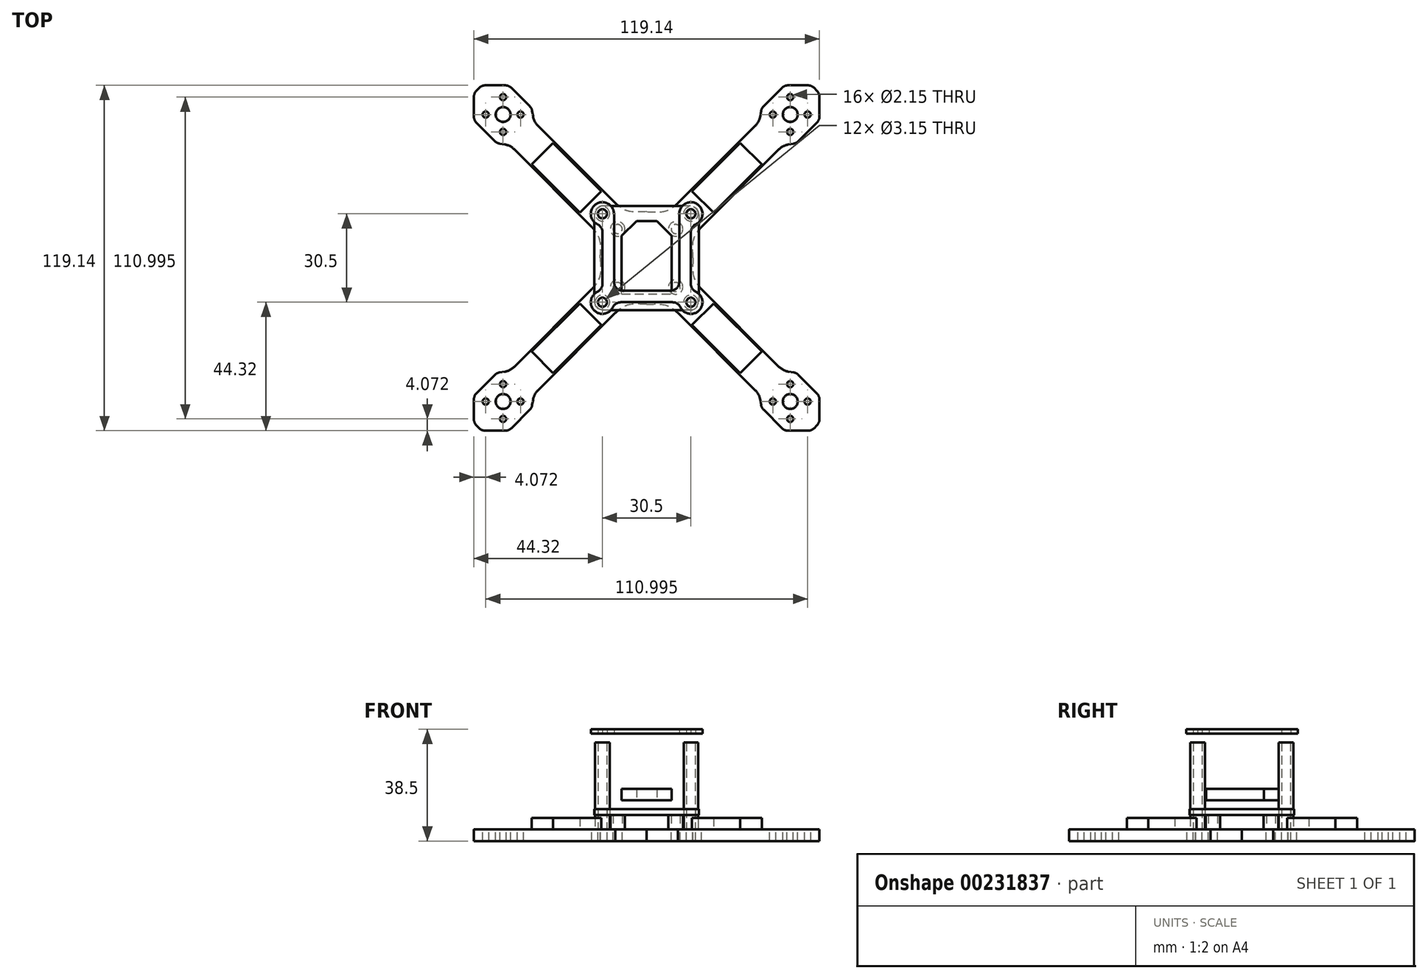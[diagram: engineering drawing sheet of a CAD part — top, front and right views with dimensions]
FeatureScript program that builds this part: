
annotation { "Feature Type Name" : "Feature", "Feature Type Description" : "" }
export const myFeature = defineFeature(function(context is Context, id is Id, definition is map)
    precondition{}
    {
        {
            var Q0;
            Q0=qCreatedBy(makeId("Top.planeOp"),FACE);
            var sketch = newSketch(context, id + "F0", { "sketchPlane" : qUnion([Q0])});
            skCircle(sketch, "E0.1", {"center": v(15.25, 15.25) * mm, "radius": 1.57 * mm});
            skLineSegment(sketch, "E1", {"start": v(49.5, 55.5) * mm, "end": v(49.5, 43.5) * mm, "construction": true});
            skLineSegment(sketch, "E2", {"start": v(45.25, 53.74) * mm, "end": v(53.74, 45.25) * mm, "construction": true});
            skCircle(sketch, "E3.MirrorC", {"center": v(49.5, 49.5) * mm, "radius": 2.58 * mm});
            skLineSegment(sketch, "E4", {"start": v(43.5, 49.5) * mm, "end": v(55.5, 49.5) * mm, "construction": true});
            skCircle(sketch, "E5", {"center": v(49.5, 49.5) * mm, "radius": 6 * mm, "construction": true});
            skCircle(sketch, "E6", {"center": v(43.5, 49.5) * mm, "radius": 1.07 * mm});
            skCircle(sketch, "E7.MirrorC", {"center": v(55.5, 49.5) * mm, "radius": 1.07 * mm});
            skCircle(sketch, "E8.MirrorC", {"center": v(49.5, 55.5) * mm, "radius": 1.07 * mm});
            skCircle(sketch, "E9.MirrorC", {"center": v(49.5, 43.5) * mm, "radius": 1.07 * mm});
            skLineSegment(sketch, "E10", {"start": v(0, 78.07) * mm, "end": v(0, -78.07) * mm, "construction": true});
            skLineSegment(sketch, "E11", {"start": v(-70, 0) * mm, "end": v(70, 0) * mm, "construction": true});
            skCircle(sketch, "E12.MirrorC", {"center": v(-15.25, 15.25) * mm, "radius": 1.57 * mm});
            skCircle(sketch, "E13.MirrorC", {"center": v(-15.25, -15.25) * mm, "radius": 1.57 * mm});
            skCircle(sketch, "E14.MirrorC", {"center": v(15.25, -15.25) * mm, "radius": 1.57 * mm});
            skLineSegment(sketch, "E15", {"start": v(49.5, 49.5) * mm, "end": v(-49.5, -49.5) * mm, "construction": true});
            skLineSegment(sketch, "E16", {"start": v(-49.5, 49.5) * mm, "end": v(49.5, -49.5) * mm, "construction": true});
            skLineSegment(sketch, "E17", {"start": v(10.78, 18.91) * mm, "end": v(18.91, 10.78) * mm, "construction": true});
            skPoint(sketch, "E18", {"position": v(14.85, 14.85) * mm});
            skPoint(sketch, "E19", {"position": v(0, 16) * mm});
            skLineSegment(sketch, "E20", {"start": v(49.5, 49.5) * mm, "end": v(67.48, 67.48) * mm, "construction": true});
            skCircle(sketch, "E21.MirrorC", {"center": v(55.5, -49.5) * mm, "radius": 1.07 * mm});
            skCircle(sketch, "E22.MirrorC", {"center": v(49.5, -43.5) * mm, "radius": 1.07 * mm});
            skLineSegment(sketch, "E23.MirrorCS", {"start": v(45.25, -53.74) * mm, "end": v(53.74, -45.25) * mm, "construction": true});
            skCircle(sketch, "E24.MirrorC", {"center": v(49.5, -55.5) * mm, "radius": 1.07 * mm});
            skLineSegment(sketch, "E25.MirrorCS", {"start": v(49.5, -55.5) * mm, "end": v(49.5, -43.5) * mm, "construction": true});
            skLineSegment(sketch, "E26.MirrorCS", {"start": v(43.5, -49.5) * mm, "end": v(55.5, -49.5) * mm, "construction": true});
            skCircle(sketch, "E27.MirrorC", {"center": v(43.5, -49.5) * mm, "radius": 1.07 * mm});
            skPoint(sketch, "E28.MirrorP", {"position": v(49.5, -49.5) * mm});
            skCircle(sketch, "E29.MirrorC", {"center": v(49.5, -49.5) * mm, "radius": 6 * mm, "construction": true});
            skCircle(sketch, "E30.MirrorC", {"center": v(49.5, -49.5) * mm, "radius": 2.58 * mm});
            skCircle(sketch, "E31.MirrorC", {"center": v(-49.5, -55.5) * mm, "radius": 1.07 * mm});
            skCircle(sketch, "E32.MirrorC", {"center": v(-43.5, -49.5) * mm, "radius": 1.07 * mm});
            skCircle(sketch, "E33.MirrorC", {"center": v(-55.5, -49.5) * mm, "radius": 1.07 * mm});
            skCircle(sketch, "E34.MirrorC", {"center": v(-49.5, -43.5) * mm, "radius": 1.07 * mm});
            skLineSegment(sketch, "E35.MirrorCS", {"start": v(-45.25, -53.74) * mm, "end": v(-53.74, -45.25) * mm, "construction": true});
            skLineSegment(sketch, "E36.MirrorCS", {"start": v(-43.5, -49.5) * mm, "end": v(-55.5, -49.5) * mm, "construction": true});
            skLineSegment(sketch, "E37.MirrorCS", {"start": v(-49.5, -55.5) * mm, "end": v(-49.5, -43.5) * mm, "construction": true});
            skPoint(sketch, "E38.MirrorP", {"position": v(-49.5, -49.5) * mm});
            skCircle(sketch, "E39.MirrorC", {"center": v(-49.5, -49.5) * mm, "radius": 6 * mm, "construction": true});
            skCircle(sketch, "E40.MirrorC", {"center": v(-49.5, -49.5) * mm, "radius": 2.58 * mm});
            skCircle(sketch, "E41.MirrorC", {"center": v(-49.5, 55.5) * mm, "radius": 1.07 * mm});
            skCircle(sketch, "E42.MirrorC", {"center": v(-43.5, 49.5) * mm, "radius": 1.07 * mm});
            skCircle(sketch, "E43.MirrorC", {"center": v(-49.5, 43.5) * mm, "radius": 1.07 * mm});
            skCircle(sketch, "E44.MirrorC", {"center": v(-55.5, 49.5) * mm, "radius": 1.07 * mm});
            skLineSegment(sketch, "E45.MirrorCS", {"start": v(-45.25, 53.74) * mm, "end": v(-53.74, 45.25) * mm, "construction": true});
            skLineSegment(sketch, "E46.MirrorCS", {"start": v(-43.5, 49.5) * mm, "end": v(-55.5, 49.5) * mm, "construction": true});
            skLineSegment(sketch, "E47.MirrorCS", {"start": v(-49.5, 55.5) * mm, "end": v(-49.5, 43.5) * mm, "construction": true});
            skPoint(sketch, "E48.MirrorP", {"position": v(-49.5, 49.5) * mm});
            skCircle(sketch, "E49.MirrorC", {"center": v(-49.5, 49.5) * mm, "radius": 6 * mm, "construction": true});
            skCircle(sketch, "E50.MirrorC", {"center": v(-49.5, 49.5) * mm, "radius": 2.58 * mm});
            skCircle(sketch, "E51.MirrorC", {"center": v(10, 10) * mm, "radius": 1.57 * mm});
            skCircle(sketch, "E52.MirrorC", {"center": v(10, -10) * mm, "radius": 1.57 * mm});
            skCircle(sketch, "E53.MirrorC", {"center": v(-10, -10) * mm, "radius": 1.57 * mm});
            skCircle(sketch, "E54.MirrorC", {"center": v(-10, 10) * mm, "radius": 1.57 * mm});
            skLineSegment(sketch, "E55", {"start": v(16, 8) * mm, "end": v(16, -8) * mm, "construction": true});
            skPoint(sketch, "E56", {"position": v(16, 0) * mm});
            skPoint(sketch, "E57", {"position": v(0, 0) * mm});
            skPoint(sketch, "E58", {"position": v(-27.66, 27.66) * mm});
            skPoint(sketch, "E59", {"position": v(6.88, 16.35) * mm});
            skFitSpline(sketch, "E60", {"points": [v(0, 16) * mm, v(6.88, 16.35) * mm, v(10.78, 18.91) * mm], "startDerivative": vector(12.86, -0.37) * mm, "endDerivative": vector(5.42, 4.33) * mm});
            skLineSegment(sketch, "E61", {"start": v(10.78, 18.91) * mm, "end": v(37.5, 45.63) * mm});
            skLineSegment(sketch, "E62", {"start": v(39.18, 48.92) * mm, "end": v(39.46, 50.68) * mm});
            skLineSegment(sketch, "E63", {"start": v(40.3, 52.33) * mm, "end": v(46.67, 58.69) * mm});
            skLineSegment(sketch, "E64", {"start": v(48.8, 59.57) * mm, "end": v(55.6, 59.57) * mm});
            skLineSegment(sketch, "E65", {"start": v(57.71, 58.69) * mm, "end": v(58.2, 58.2) * mm});
            skPoint(sketch, "E66.visualSharp", {"position": v(38.87, 47) * mm});
            skArc(sketch, "E66.filletArc", {"start": v(37.5, 45.63) * mm, "mid": v(38.6, 47.14) * mm, "end": v(39.18, 48.92) * mm});
            skPoint(sketch, "E67.visualSharp", {"position": v(39.62, 51.64) * mm});
            skArc(sketch, "E67.filletArc", {"start": v(40.3, 52.33) * mm, "mid": v(39.76, 51.57) * mm, "end": v(39.46, 50.68) * mm});
            skPoint(sketch, "E68.visualSharp", {"position": v(47.55, 59.57) * mm});
            skArc(sketch, "E68.filletArc", {"start": v(48.8, 59.57) * mm, "mid": v(47.64, 59.34) * mm, "end": v(46.67, 58.69) * mm});
            skPoint(sketch, "E69.visualSharp", {"position": v(56.84, 59.57) * mm});
            skArc(sketch, "E69.filletArc", {"start": v(57.71, 58.69) * mm, "mid": v(56.74, 59.34) * mm, "end": v(55.6, 59.57) * mm});
            skLineSegment(sketch, "E70.MirrorCS", {"start": v(52.33, 40.3) * mm, "end": v(58.69, 46.67) * mm});
            skPoint(sketch, "E71.MirrorP", {"position": v(47, 38.87) * mm});
            skArc(sketch, "E72.MirrorCS", {"start": v(52.33, 40.3) * mm, "mid": v(51.57, 39.76) * mm, "end": v(50.68, 39.46) * mm});
            skArc(sketch, "E73.MirrorCS", {"start": v(45.63, 37.5) * mm, "mid": v(47.14, 38.6) * mm, "end": v(48.92, 39.18) * mm});
            skPoint(sketch, "E74.MirrorP", {"position": v(51.64, 39.62) * mm});
            skArc(sketch, "E75.MirrorCS", {"start": v(59.57, 48.8) * mm, "mid": v(59.34, 47.64) * mm, "end": v(58.69, 46.67) * mm});
            skArc(sketch, "E76.MirrorCS", {"start": v(58.69, 57.71) * mm, "mid": v(59.34, 56.74) * mm, "end": v(59.57, 55.6) * mm});
            skPoint(sketch, "E77.MirrorP", {"position": v(59.57, 56.84) * mm});
            skLineSegment(sketch, "E78.MirrorCS", {"start": v(58.69, 57.71) * mm, "end": v(58.2, 58.2) * mm});
            skLineSegment(sketch, "E79.MirrorCS", {"start": v(59.57, 48.8) * mm, "end": v(59.57, 55.6) * mm});
            skPoint(sketch, "E80.MirrorP", {"position": v(59.57, 47.55) * mm});
            skLineSegment(sketch, "E81.MirrorCS", {"start": v(18.91, 10.78) * mm, "end": v(45.63, 37.5) * mm});
            skLineSegment(sketch, "E82.MirrorCS", {"start": v(48.92, 39.18) * mm, "end": v(50.68, 39.46) * mm});
            skFitSpline(sketch, "E83.MirrorCS", {"points": [v(16, 0) * mm, v(16.35, 6.88) * mm, v(18.91, 10.78) * mm], "startDerivative": vector(-0.37, 12.86) * mm, "endDerivative": vector(4.33, 5.42) * mm});
            skLineSegment(sketch, "E84", {"start": v(48.8, 56.57) * mm, "end": v(42.43, 50.2) * mm, "construction": true});
            skPoint(sketch, "E85", {"position": v(45.6, 53.39) * mm});
            skLineSegment(sketch, "E86.MirrorCS", {"start": v(57.71, -58.69) * mm, "end": v(58.2, -58.2) * mm});
            skLineSegment(sketch, "E87.MirrorCS", {"start": v(48.92, -39.18) * mm, "end": v(50.68, -39.46) * mm});
            skLineSegment(sketch, "E88.MirrorCS", {"start": v(39.18, -48.92) * mm, "end": v(39.46, -50.68) * mm});
            skLineSegment(sketch, "E89.MirrorCS", {"start": v(58.69, -57.71) * mm, "end": v(58.2, -58.2) * mm});
            skArc(sketch, "E90.MirrorCS", {"start": v(48.8, -59.57) * mm, "mid": v(47.64, -59.34) * mm, "end": v(46.67, -58.69) * mm});
            skArc(sketch, "E91.MirrorCS", {"start": v(37.5, -45.63) * mm, "mid": v(38.6, -47.14) * mm, "end": v(39.18, -48.92) * mm});
            skArc(sketch, "E92.MirrorCS", {"start": v(57.71, -58.69) * mm, "mid": v(56.74, -59.34) * mm, "end": v(55.6, -59.57) * mm});
            skArc(sketch, "E93.MirrorCS", {"start": v(45.63, -37.5) * mm, "mid": v(47.14, -38.6) * mm, "end": v(48.92, -39.18) * mm});
            skArc(sketch, "E94.MirrorCS", {"start": v(59.57, -48.8) * mm, "mid": v(59.34, -47.64) * mm, "end": v(58.69, -46.67) * mm});
            skArc(sketch, "E95.MirrorCS", {"start": v(52.33, -40.3) * mm, "mid": v(51.57, -39.76) * mm, "end": v(50.68, -39.46) * mm});
            skArc(sketch, "E96.MirrorCS", {"start": v(58.69, -57.71) * mm, "mid": v(59.34, -56.74) * mm, "end": v(59.57, -55.6) * mm});
            skArc(sketch, "E97.MirrorCS", {"start": v(40.3, -52.33) * mm, "mid": v(39.76, -51.57) * mm, "end": v(39.46, -50.68) * mm});
            skLineSegment(sketch, "E98.MirrorCS", {"start": v(48.8, -56.57) * mm, "end": v(42.43, -50.2) * mm, "construction": true});
            skFitSpline(sketch, "E99.MirrorCS", {"points": [v(16, 0) * mm, v(16.35, -6.88) * mm, v(18.91, -10.78) * mm], "startDerivative": vector(-0.37, -12.86) * mm, "endDerivative": vector(4.33, -5.42) * mm});
            skFitSpline(sketch, "E100.MirrorCS", {"points": [v(0, -16) * mm, v(6.88, -16.35) * mm, v(10.78, -18.91) * mm], "startDerivative": vector(12.86, 0.37) * mm, "endDerivative": vector(5.42, -4.33) * mm});
            skPoint(sketch, "E101.MirrorP", {"position": v(59.57, -47.55) * mm});
            skLineSegment(sketch, "E102.MirrorCS", {"start": v(52.33, -40.3) * mm, "end": v(58.69, -46.67) * mm});
            skLineSegment(sketch, "E103.MirrorCS", {"start": v(40.3, -52.33) * mm, "end": v(46.67, -58.69) * mm});
            skPoint(sketch, "E104.MirrorP", {"position": v(47.55, -59.57) * mm});
            skPoint(sketch, "E105.MirrorP", {"position": v(38.87, -47) * mm});
            skPoint(sketch, "E106.MirrorP", {"position": v(47, -38.87) * mm});
            skLineSegment(sketch, "E107.MirrorCS", {"start": v(10.78, -18.91) * mm, "end": v(37.5, -45.63) * mm});
            skPoint(sketch, "E108.MirrorP", {"position": v(39.62, -51.64) * mm});
            skLineSegment(sketch, "E109.MirrorCS", {"start": v(59.57, -48.8) * mm, "end": v(59.57, -55.6) * mm});
            skPoint(sketch, "E110.MirrorP", {"position": v(51.64, -39.62) * mm});
            skPoint(sketch, "E111.MirrorP", {"position": v(59.57, -56.84) * mm});
            skPoint(sketch, "E112.MirrorP", {"position": v(45.6, -53.39) * mm});
            skLineSegment(sketch, "E113.MirrorCS", {"start": v(48.8, -59.57) * mm, "end": v(55.6, -59.57) * mm});
            skPoint(sketch, "E114.MirrorP", {"position": v(56.84, -59.57) * mm});
            skLineSegment(sketch, "E115.MirrorCS", {"start": v(18.91, -10.78) * mm, "end": v(45.63, -37.5) * mm});
            skLineSegment(sketch, "E116.MirrorCS", {"start": v(-57.71, 58.69) * mm, "end": v(-58.2, 58.2) * mm});
            skLineSegment(sketch, "E117.MirrorCS", {"start": v(-58.69, -57.71) * mm, "end": v(-58.2, -58.2) * mm});
            skLineSegment(sketch, "E118.MirrorCS", {"start": v(-39.18, -48.92) * mm, "end": v(-39.46, -50.68) * mm});
            skArc(sketch, "E119.MirrorCS", {"start": v(-40.3, -52.33) * mm, "mid": v(-39.76, -51.57) * mm, "end": v(-39.46, -50.68) * mm});
            skArc(sketch, "E120.MirrorCS", {"start": v(-37.5, -45.63) * mm, "mid": v(-38.6, -47.14) * mm, "end": v(-39.18, -48.92) * mm});
            skArc(sketch, "E121.MirrorCS", {"start": v(-45.63, -37.5) * mm, "mid": v(-47.14, -38.6) * mm, "end": v(-48.92, -39.18) * mm});
            skLineSegment(sketch, "E122.MirrorCS", {"start": v(-39.18, 48.92) * mm, "end": v(-39.46, 50.68) * mm});
            skArc(sketch, "E123.MirrorCS", {"start": v(-59.57, -48.8) * mm, "mid": v(-59.34, -47.64) * mm, "end": v(-58.69, -46.67) * mm});
            skArc(sketch, "E124.MirrorCS", {"start": v(-58.69, 57.71) * mm, "mid": v(-59.34, 56.74) * mm, "end": v(-59.57, 55.6) * mm});
            skArc(sketch, "E125.MirrorCS", {"start": v(-57.71, -58.69) * mm, "mid": v(-56.74, -59.34) * mm, "end": v(-55.6, -59.57) * mm});
            skArc(sketch, "E126.MirrorCS", {"start": v(-57.71, 58.69) * mm, "mid": v(-56.74, 59.34) * mm, "end": v(-55.6, 59.57) * mm});
            skLineSegment(sketch, "E127.MirrorCS", {"start": v(-57.71, -58.69) * mm, "end": v(-58.2, -58.2) * mm});
            skLineSegment(sketch, "E128.MirrorCS", {"start": v(-48.92, 39.18) * mm, "end": v(-50.68, 39.46) * mm});
            skLineSegment(sketch, "E129.MirrorCS", {"start": v(-48.92, -39.18) * mm, "end": v(-50.68, -39.46) * mm});
            skLineSegment(sketch, "E130.MirrorCS", {"start": v(-58.69, 57.71) * mm, "end": v(-58.2, 58.2) * mm});
            skArc(sketch, "E131.MirrorCS", {"start": v(-59.57, 48.8) * mm, "mid": v(-59.34, 47.64) * mm, "end": v(-58.69, 46.67) * mm});
            skArc(sketch, "E132.MirrorCS", {"start": v(-40.3, 52.33) * mm, "mid": v(-39.76, 51.57) * mm, "end": v(-39.46, 50.68) * mm});
            skArc(sketch, "E133.MirrorCS", {"start": v(-45.63, 37.5) * mm, "mid": v(-47.14, 38.6) * mm, "end": v(-48.92, 39.18) * mm});
            skArc(sketch, "E134.MirrorCS", {"start": v(-58.69, -57.71) * mm, "mid": v(-59.34, -56.74) * mm, "end": v(-59.57, -55.6) * mm});
            skArc(sketch, "E135.MirrorCS", {"start": v(-52.33, -40.3) * mm, "mid": v(-51.57, -39.76) * mm, "end": v(-50.68, -39.46) * mm});
            skArc(sketch, "E136.MirrorCS", {"start": v(-48.8, 59.57) * mm, "mid": v(-47.64, 59.34) * mm, "end": v(-46.67, 58.69) * mm});
            skArc(sketch, "E137.MirrorCS", {"start": v(-48.8, -59.57) * mm, "mid": v(-47.64, -59.34) * mm, "end": v(-46.67, -58.69) * mm});
            skArc(sketch, "E138.MirrorCS", {"start": v(-37.5, 45.63) * mm, "mid": v(-38.6, 47.14) * mm, "end": v(-39.18, 48.92) * mm});
            skArc(sketch, "E139.MirrorCS", {"start": v(-52.33, 40.3) * mm, "mid": v(-51.57, 39.76) * mm, "end": v(-50.68, 39.46) * mm});
            skFitSpline(sketch, "E140.MirrorCS", {"points": [v(-16, 0) * mm, v(-16.35, 6.88) * mm, v(-18.91, 10.78) * mm], "startDerivative": vector(0.37, 12.86) * mm, "endDerivative": vector(-4.33, 5.42) * mm});
            skFitSpline(sketch, "E141.MirrorCS", {"points": [v(0, -16) * mm, v(-6.88, -16.35) * mm, v(-10.78, -18.91) * mm], "startDerivative": vector(-12.86, 0.37) * mm, "endDerivative": vector(-5.42, -4.33) * mm});
            skLineSegment(sketch, "E142.MirrorCS", {"start": v(-48.8, -56.57) * mm, "end": v(-42.43, -50.2) * mm, "construction": true});
            skFitSpline(sketch, "E143.MirrorCS", {"points": [v(0, 16) * mm, v(-6.88, 16.35) * mm, v(-10.78, 18.91) * mm], "startDerivative": vector(-12.86, -0.37) * mm, "endDerivative": vector(-5.42, 4.33) * mm});
            skFitSpline(sketch, "E144.MirrorCS", {"points": [v(-16, 0) * mm, v(-16.35, -6.88) * mm, v(-18.91, -10.78) * mm], "startDerivative": vector(0.37, -12.86) * mm, "endDerivative": vector(-4.33, -5.42) * mm});
            skLineSegment(sketch, "E145.MirrorCS", {"start": v(-48.8, 56.57) * mm, "end": v(-42.43, 50.2) * mm, "construction": true});
            skLineSegment(sketch, "E146.MirrorCS", {"start": v(-40.3, -52.33) * mm, "end": v(-46.67, -58.69) * mm});
            skLineSegment(sketch, "E147.MirrorCS", {"start": v(-48.8, -59.57) * mm, "end": v(-55.6, -59.57) * mm});
            skPoint(sketch, "E148.MirrorP", {"position": v(-39.62, 51.64) * mm});
            skPoint(sketch, "E149.MirrorP", {"position": v(-47.55, -59.57) * mm});
            skPoint(sketch, "E150.MirrorP", {"position": v(-45.6, -53.39) * mm});
            skLineSegment(sketch, "E151.MirrorCS", {"start": v(-49.5, 49.5) * mm, "end": v(-67.48, 67.48) * mm, "construction": true});
            skPoint(sketch, "E152.MirrorP", {"position": v(-38.87, 47) * mm});
            skLineSegment(sketch, "E153.MirrorCS", {"start": v(-10.78, 18.91) * mm, "end": v(-37.5, 45.63) * mm});
            skLineSegment(sketch, "E154.MirrorCS", {"start": v(-40.3, 52.33) * mm, "end": v(-46.67, 58.69) * mm});
            skPoint(sketch, "E155.MirrorP", {"position": v(-51.64, -39.62) * mm});
            skPoint(sketch, "E156.MirrorP", {"position": v(-59.57, 47.55) * mm});
            skLineSegment(sketch, "E157.MirrorCS", {"start": v(-52.33, -40.3) * mm, "end": v(-58.69, -46.67) * mm});
            skPoint(sketch, "E158.MirrorP", {"position": v(-56.84, 59.57) * mm});
            skPoint(sketch, "E159.MirrorP", {"position": v(-59.57, -47.55) * mm});
            skPoint(sketch, "E160.MirrorP", {"position": v(-59.57, 56.84) * mm});
            skLineSegment(sketch, "E161.MirrorCS", {"start": v(-18.91, 10.78) * mm, "end": v(-45.63, 37.5) * mm});
            skPoint(sketch, "E162.MirrorP", {"position": v(-38.87, -47) * mm});
            skLineSegment(sketch, "E163.MirrorCS", {"start": v(-59.57, 48.8) * mm, "end": v(-59.57, 55.6) * mm});
            skPoint(sketch, "E164.MirrorP", {"position": v(-47, -38.87) * mm});
            skPoint(sketch, "E165.MirrorP", {"position": v(-59.57, -56.84) * mm});
            skLineSegment(sketch, "E166.MirrorCS", {"start": v(-18.91, -10.78) * mm, "end": v(-45.63, -37.5) * mm});
            skPoint(sketch, "E167.MirrorP", {"position": v(-47, 38.87) * mm});
            skPoint(sketch, "E168.MirrorP", {"position": v(-47.55, 59.57) * mm});
            skLineSegment(sketch, "E169.MirrorCS", {"start": v(-52.33, 40.3) * mm, "end": v(-58.69, 46.67) * mm});
            skPoint(sketch, "E170.MirrorP", {"position": v(-56.84, -59.57) * mm});
            skLineSegment(sketch, "E171.MirrorCS", {"start": v(-10.78, -18.91) * mm, "end": v(-37.5, -45.63) * mm});
            skPoint(sketch, "E172.MirrorP", {"position": v(-51.64, 39.62) * mm});
            skLineSegment(sketch, "E173.MirrorCS", {"start": v(-59.57, -48.8) * mm, "end": v(-59.57, -55.6) * mm});
            skLineSegment(sketch, "E174.MirrorCS", {"start": v(-48.8, 59.57) * mm, "end": v(-55.6, 59.57) * mm});
            skPoint(sketch, "E175.MirrorP", {"position": v(-39.62, -51.64) * mm});
            skPoint(sketch, "E176.MirrorP", {"position": v(-45.6, 53.39) * mm});
            skLineSegment(sketch, "E177", {"start": v(45.25, 53.74) * mm, "end": v(40.94, 58.06) * mm, "construction": true});
            skPoint(sketch, "E178", {"position": v(43.49, 55.5) * mm});
            skSolve(sketch);
        }
        {
            var Q0;
            Q0=qCreatedBy(makeId("Top.planeOp"),FACE);
            cPlane(context, id + "F1", {"entities" : qUnion([Q0]), "cplaneType" : CPlaneType.OFFSET, "offset" : 20 * mm, "width" : 150 * mm, "height" : 150 * mm});
        }
        {
            var Q0;
            Q0 = qSketchRegion(id + "F0", true);
            extrude(context, id + "F2", {"entities" : qUnion([Q0]), "oppositeDirection" : true, "depth" : 4 * mm, "offsetDistance" : 25 * mm});
        }
        {
            var Q0;
            Q0=qCreatedBy(makeId("Top.planeOp"),FACE);
            cPlane(context, id + "F3", {"entities" : qUnion([Q0]), "cplaneType" : CPlaneType.OFFSET, "offset" : 10 * mm, "width" : 150 * mm, "height" : 150 * mm});
        }
        {
            var Q0;
            Q0=qCreatedBy(id+"F3.planeOp",FACE);
            var sketch = newSketch(context, id + "F4", { "sketchPlane" : qUnion([Q0])});
            skLineSegment(sketch, "E179", {"start": v(-8.62, -12.37) * mm, "end": v(8.63, -12.37) * mm});
            skLineSegment(sketch, "E180", {"start": v(-8.62, -12.37) * mm, "end": v(-8.62, 7.63) * mm});
            skLineSegment(sketch, "E181", {"start": v(0, -12.37) * mm, "end": v(0, 12.78) * mm, "construction": true});
            skPoint(sketch, "E181.startSnap0", {"position": v(0, -12.37) * mm});
            skLineSegment(sketch, "E182", {"start": v(-3.5, 12.78) * mm, "end": v(3.5, 12.78) * mm});
            skPoint(sketch, "E183", {"position": v(0, 12.78) * mm});
            skLineSegment(sketch, "E184", {"start": v(-8.62, 7.63) * mm, "end": v(-3.5, 12.78) * mm});
            skLineSegment(sketch, "E185.MirrorCS", {"start": v(8.63, 7.63) * mm, "end": v(3.5, 12.78) * mm});
            skLineSegment(sketch, "E186.MirrorCS", {"start": v(8.63, -12.37) * mm, "end": v(8.63, 7.63) * mm});
            skSolve(sketch);
        }
        {
            var Q0;
            Q0 = qSketchRegion(id + "F4", true);
            extrude(context, id + "F5", {"entities" : qUnion([Q0]), "depth" : 4 * mm});
        }
        {
            var Q0;
            Q0=qCreatedBy(makeId("Top.planeOp"),FACE);
            cPlane(context, id + "F6", {"entities" : qUnion([Q0]), "cplaneType" : CPlaneType.OFFSET, "offset" : 5 * mm, "width" : 150 * mm, "height" : 150 * mm});
        }
        {
            var Q0;
            Q0=qCreatedBy(id+"F6.planeOp",FACE);
            var sketch = newSketch(context, id + "F7", { "sketchPlane" : qUnion([Q0])});
            skLineSegment(sketch, "E187", {"start": v(0, 13.5) * mm, "end": v(0, -13.5) * mm, "construction": true});
            skLineSegment(sketch, "E188", {"start": v(-13.5, 0) * mm, "end": v(13.5, 0) * mm, "construction": true});
            skLineSegment(sketch, "E189", {"start": v(-13.5, 10.5) * mm, "end": v(-13.5, -10.5) * mm});
            skLineSegment(sketch, "E190", {"start": v(10.5, 13.5) * mm, "end": v(-10.5, 13.5) * mm});
            skLineSegment(sketch, "E191.MirrorCS", {"start": v(10.5, -13.5) * mm, "end": v(-10.5, -13.5) * mm});
            skLineSegment(sketch, "E192.MirrorCS", {"start": v(13.5, 10.5) * mm, "end": v(13.5, -10.5) * mm});
            skLineSegment(sketch, "E193", {"start": v(-10.5, 13.5) * mm, "end": v(-13.5, 10.5) * mm});
            skLineSegment(sketch, "E194.MirrorCS", {"start": v(-10.5, -13.5) * mm, "end": v(-13.5, -10.5) * mm});
            skLineSegment(sketch, "E195.MirrorCS", {"start": v(10.5, 13.5) * mm, "end": v(13.5, 10.5) * mm});
            skLineSegment(sketch, "E196.MirrorCS", {"start": v(10.5, -13.5) * mm, "end": v(13.5, -10.5) * mm});
            skCircle(sketch, "E197", {"center": v(-10, 10) * mm, "radius": 1.57 * mm});
            skLineSegment(sketch, "E198", {"start": v(-10, 10) * mm, "end": v(10, 10) * mm, "construction": true});
            skLineSegment(sketch, "E199", {"start": v(10, 10) * mm, "end": v(10, -10) * mm, "construction": true});
            skLineSegment(sketch, "E200", {"start": v(10, -10) * mm, "end": v(-10, -10) * mm, "construction": true});
            skLineSegment(sketch, "E201", {"start": v(-10, -10) * mm, "end": v(-10, 10) * mm, "construction": true});
            skPoint(sketch, "E202", {"position": v(0, 10) * mm});
            skPoint(sketch, "E203", {"position": v(-10, 0) * mm});
            skCircle(sketch, "E204.MirrorC", {"center": v(10, 10) * mm, "radius": 1.57 * mm});
            skCircle(sketch, "E205.MirrorC", {"center": v(-10, -10) * mm, "radius": 1.57 * mm});
            skCircle(sketch, "E206.MirrorC", {"center": v(10, -10) * mm, "radius": 1.57 * mm});
            skSolve(sketch);
        }
        {
            var Q0;
            Q0 = qSketchRegion(id + "F7", true);
            extrude(context, id + "F8", {"entities" : qUnion([Q0]), "depth" : 2 * mm});
        }
        {
            var Q0;
            Q0=qCreatedBy(id+"F6.planeOp",FACE);
            var sketch = newSketch(context, id + "F9", { "sketchPlane" : qUnion([Q0])});
            skLineSegment(sketch, "E207", {"start": v(0, 18) * mm, "end": v(0, -18) * mm, "construction": true});
            skLineSegment(sketch, "E208", {"start": v(-18, 0) * mm, "end": v(18, 0) * mm, "construction": true});
            skCircle(sketch, "E209", {"center": v(-15.25, 15.25) * mm, "radius": 1.57 * mm});
            skLineSegment(sketch, "E210", {"start": v(-15.25, 15.25) * mm, "end": v(15.25, 15.25) * mm, "construction": true});
            skLineSegment(sketch, "E211", {"start": v(15.25, 15.25) * mm, "end": v(15.25, -15.25) * mm, "construction": true});
            skLineSegment(sketch, "E212", {"start": v(15.25, -15.25) * mm, "end": v(-15.25, -15.25) * mm, "construction": true});
            skLineSegment(sketch, "E213", {"start": v(-15.25, -15.25) * mm, "end": v(-15.25, 15.25) * mm, "construction": true});
            skPoint(sketch, "E214", {"position": v(0, 15.25) * mm});
            skPoint(sketch, "E215", {"position": v(-15.25, 0) * mm});
            skCircle(sketch, "E216.MirrorC", {"center": v(15.25, 15.25) * mm, "radius": 1.57 * mm});
            skCircle(sketch, "E217.MirrorC", {"center": v(-15.25, -15.25) * mm, "radius": 1.57 * mm});
            skCircle(sketch, "E218.MirrorC", {"center": v(15.25, -15.25) * mm, "radius": 1.57 * mm});
            skPoint(sketch, "E219", {"position": v(0, 0) * mm});
            skLineSegment(sketch, "E220.bottom", {"start": v(15, 18) * mm, "end": v(-15, 18) * mm});
            skLineSegment(sketch, "E220.top", {"start": v(15, -18) * mm, "end": v(-15, -18) * mm});
            skLineSegment(sketch, "E220.left", {"start": v(18, 15) * mm, "end": v(18, -15) * mm});
            skLineSegment(sketch, "E220.right", {"start": v(-18, 15) * mm, "end": v(-18, -15) * mm});
            skPoint(sketch, "E221.visualSharp", {"position": v(-18, 18) * mm});
            skArc(sketch, "E221.filletArc", {"start": v(-15, 18) * mm, "mid": v(-17.12, 17.12) * mm, "end": v(-18, 15) * mm});
            skPoint(sketch, "E222.visualSharp", {"position": v(18, 18) * mm});
            skArc(sketch, "E222.filletArc", {"start": v(18, 15) * mm, "mid": v(17.12, 17.12) * mm, "end": v(15, 18) * mm});
            skPoint(sketch, "E223.visualSharp", {"position": v(18, -18) * mm});
            skArc(sketch, "E223.filletArc", {"start": v(15, -18) * mm, "mid": v(17.12, -17.12) * mm, "end": v(18, -15) * mm});
            skPoint(sketch, "E224.visualSharp", {"position": v(-18, -18) * mm});
            skArc(sketch, "E224.filletArc", {"start": v(-18, -15) * mm, "mid": v(-17.12, -17.12) * mm, "end": v(-15, -18) * mm});
            skSolve(sketch);
        }
        {
            var Q0;
            Q0 = qSketchRegion(id + "F9", true);
            extrude(context, id + "F10", {"entities" : qUnion([Q0]), "depth" : 2 * mm, "offsetDistance" : 25 * mm});
        }
        {
            var Q0;
            Q0=qCreatedBy(makeId("Top.planeOp"),FACE);
            var sketch = newSketch(context, id + "F11", { "sketchPlane" : qUnion([Q0])});
            skLineSegment(sketch, "E225.bottom", {"start": v(-39.68, 32.25) * mm, "end": v(-32.25, 39.68) * mm});
            skLineSegment(sketch, "E225.top", {"start": v(-23.06, 15.64) * mm, "end": v(-15.64, 23.06) * mm});
            skLineSegment(sketch, "E225.left", {"start": v(-39.68, 32.25) * mm, "end": v(-23.06, 15.64) * mm});
            skLineSegment(sketch, "E225.right", {"start": v(-32.25, 39.68) * mm, "end": v(-15.64, 23.06) * mm});
            skLineSegment(sketch, "E226", {"start": v(-23.95, 31.37) * mm, "end": v(-31.37, 23.95) * mm, "construction": true});
            skLineSegment(sketch, "E227.MirrorCS", {"start": v(23.95, 31.37) * mm, "end": v(31.37, 23.95) * mm, "construction": true});
            skLineSegment(sketch, "E228.MirrorCS", {"start": v(23.06, 15.64) * mm, "end": v(15.64, 23.06) * mm});
            skLineSegment(sketch, "E229.MirrorCS", {"start": v(39.68, 32.25) * mm, "end": v(32.25, 39.68) * mm});
            skLineSegment(sketch, "E230.MirrorCS", {"start": v(39.68, 32.25) * mm, "end": v(23.06, 15.64) * mm});
            skLineSegment(sketch, "E231.MirrorCS", {"start": v(32.25, 39.68) * mm, "end": v(15.64, 23.06) * mm});
            skLineSegment(sketch, "E232.MirrorCS", {"start": v(23.06, -15.64) * mm, "end": v(15.64, -23.06) * mm});
            skLineSegment(sketch, "E233.MirrorCS", {"start": v(32.25, -39.68) * mm, "end": v(15.64, -23.06) * mm});
            skLineSegment(sketch, "E234.MirrorCS", {"start": v(39.68, -32.25) * mm, "end": v(32.25, -39.68) * mm});
            skLineSegment(sketch, "E235.MirrorCS", {"start": v(39.68, -32.25) * mm, "end": v(23.06, -15.64) * mm});
            skLineSegment(sketch, "E236.MirrorCS", {"start": v(-39.68, -32.25) * mm, "end": v(-23.06, -15.64) * mm});
            skLineSegment(sketch, "E237.MirrorCS", {"start": v(-23.06, -15.64) * mm, "end": v(-15.64, -23.06) * mm});
            skLineSegment(sketch, "E238.MirrorCS", {"start": v(23.95, -31.37) * mm, "end": v(31.37, -23.95) * mm, "construction": true});
            skLineSegment(sketch, "E239.MirrorCS", {"start": v(-32.25, -39.68) * mm, "end": v(-15.64, -23.06) * mm});
            skLineSegment(sketch, "E240.MirrorCS", {"start": v(-23.95, -31.37) * mm, "end": v(-31.37, -23.95) * mm, "construction": true});
            skLineSegment(sketch, "E241.MirrorCS", {"start": v(-39.68, -32.25) * mm, "end": v(-32.25, -39.68) * mm});
            skSolve(sketch);
        }
        {
            var Q0;
            Q0 = qSketchRegion(id + "F11", true);
            extrude(context, id + "F12", {"entities" : qUnion([Q0]), "operationType" : NewBodyOperationType.ADD, "depth" : 4 * mm, "offsetDistance" : 25 * mm});
        }
        {
            var Q0;
            Q0=qCreatedBy(makeId("Top.planeOp"),FACE);
            var sketch = newSketch(context, id + "F13", { "sketchPlane" : qUnion([Q0])});
            skCircle(sketch, "E242", {"center": v(15.25, 15.25) * mm, "radius": 2.5 * mm});
            skCircle(sketch, "E243.MirrorC", {"center": v(15.25, -15.25) * mm, "radius": 2.5 * mm});
            skCircle(sketch, "E244.MirrorC", {"center": v(-15.25, -15.25) * mm, "radius": 2.5 * mm});
            skCircle(sketch, "E245.MirrorC", {"center": v(-15.25, 15.25) * mm, "radius": 2.5 * mm});
            skCircle(sketch, "E246", {"center": v(15.25, 15.25) * mm, "radius": 1.55 * mm});
            skCircle(sketch, "E247.MirrorC", {"center": v(-15.25, 15.25) * mm, "radius": 1.55 * mm});
            skCircle(sketch, "E248.MirrorC", {"center": v(15.25, -15.25) * mm, "radius": 1.55 * mm});
            skCircle(sketch, "E249.MirrorC", {"center": v(-15.25, -15.25) * mm, "radius": 1.55 * mm});
            skSolve(sketch);
        }
        {
            var Q0;
            Q0 = qSketchRegion(id + "F13", true);
            extrude(context, id + "F14", {"entities" : qUnion([Q0]), "depth" : 30 * mm, "offsetDistance" : 25 * mm});
        }
        {
            var Q0;
            Q0=qCreatedBy(makeId("Top.planeOp"),FACE);
            var sketch = newSketch(context, id + "F15", { "sketchPlane" : qUnion([Q0])});
            skCircle(sketch, "E250", {"center": v(10, 10) * mm, "radius": 2.5 * mm});
            skCircle(sketch, "E251.MirrorC", {"center": v(10, -10) * mm, "radius": 2.5 * mm});
            skCircle(sketch, "E252.MirrorC", {"center": v(-10, -10) * mm, "radius": 2.5 * mm});
            skCircle(sketch, "E253.MirrorC", {"center": v(-10, 10) * mm, "radius": 2.5 * mm});
            skCircle(sketch, "E254", {"center": v(10, 10) * mm, "radius": 1.55 * mm});
            skCircle(sketch, "E255.MirrorC", {"center": v(10, -10) * mm, "radius": 1.55 * mm});
            skCircle(sketch, "E256.MirrorC", {"center": v(-10, 10) * mm, "radius": 1.55 * mm});
            skCircle(sketch, "E257.MirrorC", {"center": v(-10, -10) * mm, "radius": 1.55 * mm});
            skSolve(sketch);
        }
        {
            var Q0;
            Q0 = qSketchRegion(id + "F15", true);
            extrude(context, id + "F16", {"entities" : qUnion([Q0]), "operationType" : NewBodyOperationType.ADD, "depth" : 5 * mm, "offsetDistance" : 25 * mm});
        }
        {
            var Q0;
            Q0=qCreatedBy(makeId("Top.planeOp"),FACE);
            cPlane(context, id + "F17", {"entities" : qUnion([Q0]), "cplaneType" : CPlaneType.OFFSET, "offset" : 33 * mm, "width" : 150 * mm, "height" : 150 * mm});
        }
        {
            var Q0;
            Q0=qCreatedBy(id+"F17.planeOp",FACE);
            var sketch = newSketch(context, id + "F18", { "sketchPlane" : qUnion([Q0])});
            skLineSegment(sketch, "E258", {"start": v(15.25, 15.25) * mm, "end": v(-15.25, 15.25) * mm, "construction": true});
            skLineSegment(sketch, "E259", {"start": v(-15.25, 15.25) * mm, "end": v(-15.25, -15.25) * mm, "construction": true});
            skLineSegment(sketch, "E260", {"start": v(-15.25, -15.25) * mm, "end": v(15.25, -15.25) * mm, "construction": true});
            skLineSegment(sketch, "E261", {"start": v(15.25, -15.25) * mm, "end": v(15.25, 15.25) * mm, "construction": true});
            skArc(sketch, "E262", {"start": v(-11.25, 15.25) * mm, "mid": v(-17.39, 18.63) * mm, "end": v(-16.96, 11.64) * mm});
            skCircle(sketch, "E263", {"center": v(-15.25, 15.25) * mm, "radius": 1.57 * mm});
            skCircle(sketch, "E264.MirrorC", {"center": v(15.25, 15.25) * mm, "radius": 1.57 * mm});
            skArc(sketch, "E265.MirrorCS", {"start": v(11.25, 15.25) * mm, "mid": v(17.39, 18.63) * mm, "end": v(16.96, 11.64) * mm});
            skLineSegment(sketch, "E266.MirrorCS", {"start": v(8.93, -15.25) * mm, "end": v(-8.93, -15.25) * mm});
            skArc(sketch, "E267.MirrorCS", {"start": v(11.64, -16.96) * mm, "mid": v(18.08, -18.08) * mm, "end": v(16.96, -11.64) * mm});
            skCircle(sketch, "E268.MirrorC", {"center": v(15.25, -15.25) * mm, "radius": 1.57 * mm});
            skCircle(sketch, "E269.MirrorC", {"center": v(-15.25, -15.25) * mm, "radius": 1.57 * mm});
            skArc(sketch, "E270.MirrorCS", {"start": v(-11.64, -16.96) * mm, "mid": v(-18.08, -18.08) * mm, "end": v(-16.96, -11.64) * mm});
            skLineSegment(sketch, "E271", {"start": v(-15.25, 8.93) * mm, "end": v(-15.25, -8.93) * mm});
            skLineSegment(sketch, "E272.MirrorCS", {"start": v(15.25, 8.93) * mm, "end": v(15.25, -8.93) * mm});
            skLineSegment(sketch, "E273", {"start": v(11.25, 15.25) * mm, "end": v(11.25, -8.25) * mm});
            skLineSegment(sketch, "E274.MirrorCS", {"start": v(-11.25, 15.25) * mm, "end": v(-11.25, -8.25) * mm});
            skLineSegment(sketch, "E275", {"start": v(-8.25, -11.25) * mm, "end": v(8.25, -11.25) * mm});
            skPoint(sketch, "E276.visualSharp", {"position": v(-15.25, 11.25) * mm});
            skArc(sketch, "E276.filletArc", {"start": v(-15.25, 8.93) * mm, "mid": v(-15.71, 10.53) * mm, "end": v(-16.96, 11.64) * mm});
            skPoint(sketch, "E277.visualSharp", {"position": v(-15.25, -11.25) * mm});
            skArc(sketch, "E277.filletArc", {"start": v(-16.96, -11.64) * mm, "mid": v(-15.71, -10.53) * mm, "end": v(-15.25, -8.93) * mm});
            skPoint(sketch, "E278.visualSharp", {"position": v(-11.25, -15.25) * mm});
            skArc(sketch, "E278.filletArc", {"start": v(-8.93, -15.25) * mm, "mid": v(-10.53, -15.71) * mm, "end": v(-11.64, -16.96) * mm});
            skPoint(sketch, "E279.visualSharp", {"position": v(-11.25, -11.25) * mm});
            skArc(sketch, "E279.filletArc", {"start": v(-11.25, -8.25) * mm, "mid": v(-10.37, -10.37) * mm, "end": v(-8.25, -11.25) * mm});
            skPoint(sketch, "E280.visualSharp", {"position": v(11.25, -11.25) * mm});
            skArc(sketch, "E280.filletArc", {"start": v(8.25, -11.25) * mm, "mid": v(10.37, -10.37) * mm, "end": v(11.25, -8.25) * mm});
            skPoint(sketch, "E281.visualSharp", {"position": v(11.25, -15.25) * mm});
            skArc(sketch, "E281.filletArc", {"start": v(11.64, -16.96) * mm, "mid": v(10.53, -15.71) * mm, "end": v(8.93, -15.25) * mm});
            skPoint(sketch, "E282.visualSharp", {"position": v(15.25, -11.25) * mm});
            skArc(sketch, "E282.filletArc", {"start": v(15.25, -8.93) * mm, "mid": v(15.71, -10.53) * mm, "end": v(16.96, -11.64) * mm});
            skPoint(sketch, "E283.visualSharp", {"position": v(15.25, 11.25) * mm});
            skArc(sketch, "E283.filletArc", {"start": v(16.96, 11.64) * mm, "mid": v(15.71, 10.53) * mm, "end": v(15.25, 8.93) * mm});
            skLineSegment(sketch, "E284", {"start": v(-15.25, -4.8) * mm, "end": v(-11.25, -4.8) * mm, "construction": true});
            skLineSegment(sketch, "E285", {"start": v(-4.76, -11.25) * mm, "end": v(-4.76, -15.25) * mm, "construction": true});
            skSolve(sketch);
        }
        {
            var Q0;
            Q0 = qSketchRegion(id + "F18", true);
            extrude(context, id + "F19", {"entities" : qUnion([Q0]), "depth" : 1.5 * mm, "offsetDistance" : 25 * mm});
        }
    });
